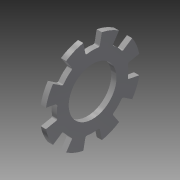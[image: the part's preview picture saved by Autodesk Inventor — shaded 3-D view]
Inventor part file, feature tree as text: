
AUTODESK INVENTOR PART (.ipt)
format: ipt  version: 2018 (Build 220112000, 112)  size: 152,064 bytes
history: native  units: mm (DEFAULTED — no unit token found)
features: sketch x2, extrude x1, pattern_circular x1
ambient origin geometry x8: Origin, YZ Plane, XZ Plane, XY Plane, X Axis, Y Axis, Z Axis, Center Point
bodies: Solid1 (feature_tree), Body (feature_tree)
feature tree (4):
  extrude  "Cut"  Depth=6.5024mm
  pattern_circular  "Cuts"  [2 undecoded]
  sketch  "Sketch1"  dims[d0=12.954mm d1=6.5024mm]
  sketch  "Sketch2"  dims[d2=0.7112mm d3=0.0mm d4=22.5deg d5=9.7282mm d6=0.7112mm d7=0.0mm d8=0.19431mm d9=80.0mm d11=360.0deg d12=0.0mm d13=0.0mm]
note: 2 required parameter values undecoded (feature->parameter linkage not recoverable at this tier; creation-order binding heuristic only, values carry confidence <= 0.55)
